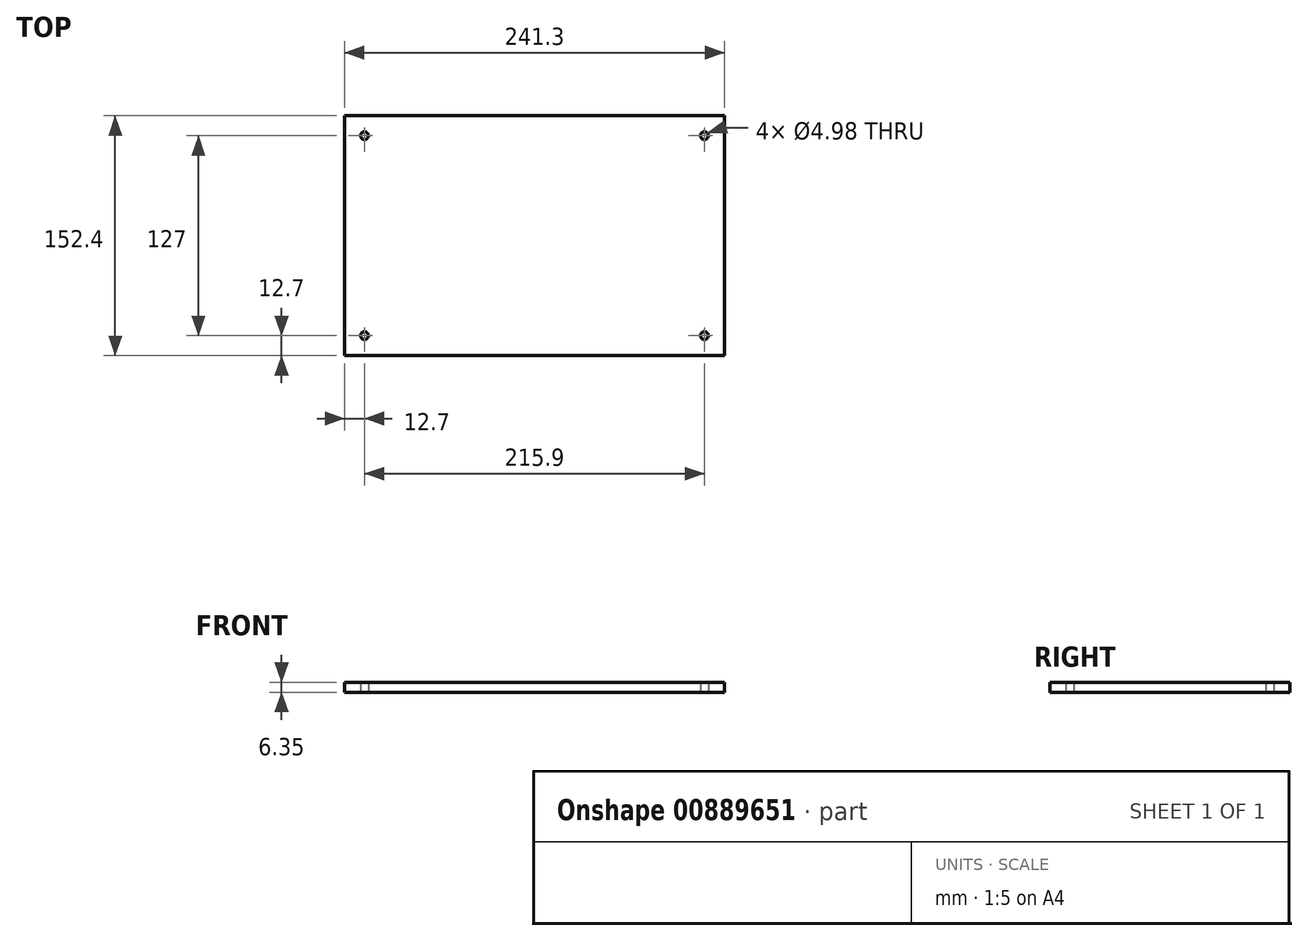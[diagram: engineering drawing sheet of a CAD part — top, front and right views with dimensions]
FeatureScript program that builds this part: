
annotation { "Feature Type Name" : "Feature", "Feature Type Description" : "" }
export const myFeature = defineFeature(function(context is Context, id is Id, definition is map)
    precondition{}
    {
        {
            var Q0;
            Q0=qCreatedBy(makeId("Top.planeOp"),FACE);
            var sketch = newSketch(context, id + "F0", { "sketchPlane" : qUnion([Q0])});
            skLineSegment(sketch, "E0.bottom", {"start": v(0, 0) * mm, "end": v(241.3, 0) * mm});
            skLineSegment(sketch, "E0.top", {"start": v(0, 152.4) * mm, "end": v(241.3, 152.4) * mm});
            skLineSegment(sketch, "E0.left", {"start": v(0, 0) * mm, "end": v(0, 152.4) * mm});
            skLineSegment(sketch, "E0.right", {"start": v(241.3, 0) * mm, "end": v(241.3, 152.4) * mm});
            skCircle(sketch, "E1", {"center": v(12.7, 12.7) * mm, "radius": 2.49 * mm});
            skCircle(sketch, "E2.0.1.0", {"center": v(12.7, 139.7) * mm, "radius": 2.49 * mm});
            skCircle(sketch, "E2.1.0.0", {"center": v(228.6, 12.7) * mm, "radius": 2.49 * mm});
            skCircle(sketch, "E2.1.1.0", {"center": v(228.6, 139.7) * mm, "radius": 2.49 * mm});
            skLineSegment(sketch, "E2.direction1", {"start": v(12.7, 12.7) * mm, "end": v(228.6, 12.7) * mm, "construction": true});
            skLineSegment(sketch, "E2.direction2", {"start": v(12.7, 12.7) * mm, "end": v(12.7, 139.7) * mm, "construction": true});
            skSolve(sketch);
        }
        {
            var Q0;
            Q0=makeQuery(id+"F0.imprint","IMPRINT",FACE,{"disambiguationData":[TD([[makeQuery(id+"F0.imprint","IMPRINT",EDGE,{"derivedFrom":sQuery(id+"F0.wireOp",EDGE,"E0.bottom")}),1.0]])]});
            extrude(context, id + "F1", {"entities" : qUnion([Q0]), "depth" : 6.35 * mm, "offsetDistance" : 25.4 * mm});
        }
    });
